# Revit family: Plumbing-Fixtures_Grohe_Rainshower_SmartControl-360-DUE_26250000_14_METRIC
name_source: partatom
category: Plumbing Fixtures
revit_build: Autodesk Revit 2014 (Build: 20130308_1515(x64)
units: mm (PartAtom-declared; Revit-internal decimal feet)

## types (1)
- Plumbing-Fixtures_Grohe_Rainshower_SmartControl-360-DUE_26250000_14_METRIC
    ADA Compliant = No
    Assembly Code = C1030220
    AssetType = Fixed
    CW Connection = Yes
    CWFU = 4.5
    ClassificationName = Uniclass 2015
    ClassificationValue = Pr_40_20_87_75
    Cold Water Connection Diameter = 10 mm  [stored 0.0328084 ft]
    Color = Chrome
    Cost = 0 $
    Default Elevation = 600 mm
    Description = Rainshower System SmartControl 360 DUO. Shower system with thermostat for wall mounting consisting of: horizontal 500 mm shower arm, exposed SmartControl thermostat. allows change between: head shower Rainshower 360 DUO, GROHE PureRain/GROHE Rain O2 spray* and TrioMassage, hand shower Power&Soul 115 (27 669 000), hand shower wall holder (27 055 000), Silverflex shower hose 1750 mm (28 388 000).
    DocumentationMaintenance = http://d3unq1hljpybmw.cloudfront.net
    DocumentationTechnical = http://d3unq1hljpybmw.cloudfront.net
    DurationUnit = Years
    Ecojoy = No
    ExpectedLife = 0
    Faucet Material = Grohe-Chrome
    Features = GROHE DreamSpray® perfect spray pattern. GROHE StarLight® chrome finish. GROHE CoolTouch® no risk of scalding. GROHE TurboStat® compact cartridge with wax thermoelement. GROHE EcoJoy® technology for less water and perfect flow. GROHE SafeStop at 38°C
    Finish = Chrome
    HW Connection = Yes
    HWFU = 4.5
    Height = 1006 mm  [stored 3.30052 ft]
    Hot Water Connection Diameter = 10 mm  [stored 0.0328084 ft]
    Keynote = N13
    Length = 500 mm  [stored 1.64042 ft]
    Low Emitting Material = No
    Manufacturer = Grohe Limited
    Masterformat Number = 01 52 19
    Masterformat Title = Sanitary Facilities
    Material = Chrome
    Model = BauEdge - Single-Lever Basin Mixer
    ModelNumber = Rainshower - 26250000
    NBSDescription = Shower fittings package;
    NBSObjectName = Shower fittings package;
    NBSReference = 45-35-70/330
    Product Documentation Link = http://www.grohe.com
    Product Page URL = http://www.grohe.com
    ProductionYear = 2016
    Size = 351x500x1006mm
    Type Comments = Rainshower - 26250000
    TypeName = BauEdge - Single-Lever Basin Mixer
    URL = www.grohe.com
    Vent Connection = No
    WFU = 0
    WarrantyDurationUnit = Years
    Waste Connection = No
    Width = 351 mm  [stored 1.15157 ft]
    _BIMspec_GUID = 0
    _current revision = 1
    _distributed by = www.bimstore.co.uk

note: [stored X ft] marks values corroborated as IEEE doubles in the binary element streams (Revit-internal decimal feet)

## geometry (parser evidence)
native form markers: Blend x6, Sweep x1
no freeform markers — native parametric forms only
